# Revit family: Vitra-Sento-WashbasinCabinet-60824-60830-60836
name_source: partatom
category: Furniture Systems
units: mm (PartAtom-declared; Revit-internal decimal feet)

## family parameters
Cut with Voids When Loaded = No
Host = Face
OmniClass Number = 23.40.00.00
OmniClass Title = Equipment and Furnishings
Part Type = Normal
Room Calculation Point = No
Round Connector Dimension = Use Diameter
Shared = Yes

## types (3) — shared parameters
BIMobject category = Bathroom compound units
Construction Type = Wall Mounted
Default Elevation = 850 mm  [stored 2.78871 ft]
Depth = 485 mm  [stored 1.59121 ft]
Description = Sento Washbasin Unit, 80 cm, with 2 drawers, without legs
Design country = Turkey
Height = 615 mm  [stored 2.01772 ft]
IFC Classification = Furniture
Installation instructions = https://cdn.vitra.com.tr
Manufacturer = Vitra
Manufacturer name = Vitra
Masterformat 2014 Code = 13 42 13
Masterformat 2014 Description = Bathroom Unit Modules
NBS Reference Code = 35-75-08
NBS Reference Description = Bathroom Cabinets
OmniClass Code = 23-31 25 13
OmniClass Description = Bathroom Cabinets
Product Guid = https://cdn.vitra.com.tr
Product certification = https://vitraglobal.com
Product data url = https://www.vitraglobal.com
Product family = Sento
Product group = Washbasin Unit
Secondary Material = Vitra-Light Oak
Technical description = https://www.vitraglobal.com
UNSPSC Code = 301815
UNSPSC Description = Bathroom Cabinets
URL = https://vitraglobal.com
Uniclass 1.4 Code = L8241
Uniclass 1.4 Description = Bathroom Cabinets
Uniclass 2.0 Code = PR-35-75-08
Uniclass 2.0 Description = Bathroom Cabinets
Uniclass 2015 Code = Pr_40_20_93
Uniclass 2015 Name = Wash basins, sinks and troughs
Uniformat II Code = E20
Uniformat II Description = FURNISHINGS
Voltage = 220 V
Warranty Period (Year) = 2
Weight Net (kg) = 62,146
Width = 780 mm  [stored 2.55906 ft]
Youtube = https://www.youtube.com
zero-valued in all types: Nominal height, Nominal width

## per-type parameters (varying)
| type | Article No. (default) | Color | Model | Primary Material | Product SKU |
| Vitra_Sento_Washbasin Unit, 80 cm, with 2 drawers, without legs, Matte White_60824 | 60824 | Matte White | 60824 | Vitra-MattWhite | 60824 |
| Vitra_Sento_Washbasin Unit, 80 cm, with 2 drawers, without legs, Matte Cream_60830 | 60830 | Matte Cream | 60830 | Vitra-Metal | 60830 |
| Vitra_Sento_Washbasin Unit, 80 cm, with 2 drawers, without legs, Matte Anthracite_60836 | 60836 | Matte Anthracite | 60836 | Vitra-DarkOlive | 60836 |

note: [stored X ft] marks values corroborated as IEEE doubles in the binary element streams (Revit-internal decimal feet)

## geometry (parser evidence)
native form markers: Sweep x3
no freeform markers — native parametric forms only
